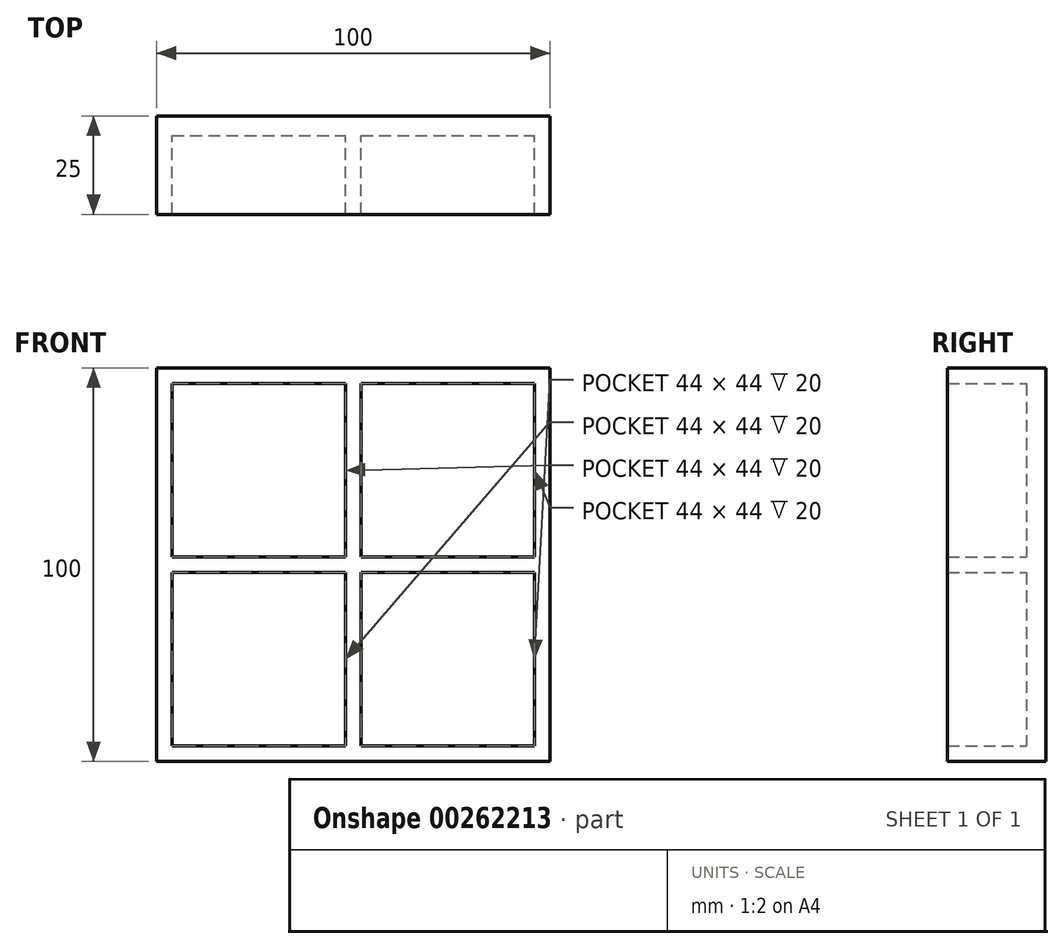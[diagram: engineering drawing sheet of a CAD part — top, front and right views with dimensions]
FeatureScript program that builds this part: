
annotation { "Feature Type Name" : "Feature", "Feature Type Description" : "" }
export const myFeature = defineFeature(function(context is Context, id is Id, definition is map)
    precondition{}
    {
        {
            var Q0;
            Q0=qCreatedBy(makeId("Front.planeOp"),FACE);
            var sketch = newSketch(context, id + "F0", { "sketchPlane" : qUnion([Q0])});
            skLineSegment(sketch, "E0.bottom", {"start": v(-54.06, 49.35) * mm, "end": v(45.94, 49.35) * mm});
            skLineSegment(sketch, "E0.top", {"start": v(-54.06, -50.65) * mm, "end": v(45.94, -50.65) * mm});
            skLineSegment(sketch, "E0.left", {"start": v(-54.06, 49.35) * mm, "end": v(-54.06, -50.65) * mm});
            skLineSegment(sketch, "E0.right", {"start": v(45.94, 49.35) * mm, "end": v(45.94, -50.65) * mm});
            skLineSegment(sketch, "E1", {"start": v(-6.06, 45.35) * mm, "end": v(-6.06, 1.35) * mm});
            skLineSegment(sketch, "E2", {"start": v(-2.06, 45.35) * mm, "end": v(-2.06, 1.35) * mm});
            skLineSegment(sketch, "E3", {"start": v(-50.06, 1.35) * mm, "end": v(-6.06, 1.35) * mm});
            skLineSegment(sketch, "E4", {"start": v(-50.06, -2.65) * mm, "end": v(-6.06, -2.65) * mm});
            skLineSegment(sketch, "E5.trimOffspring", {"start": v(-6.06, -2.65) * mm, "end": v(-6.06, -46.65) * mm});
            skLineSegment(sketch, "E6.trimOffspring", {"start": v(-2.06, 1.35) * mm, "end": v(41.94, 1.35) * mm});
            skLineSegment(sketch, "E7.trimOffspring", {"start": v(-2.06, -2.65) * mm, "end": v(-2.06, -46.65) * mm});
            skLineSegment(sketch, "E8.trimOffspring", {"start": v(-2.06, -2.65) * mm, "end": v(41.94, -2.65) * mm});
            skLineSegment(sketch, "E9", {"start": v(-50.06, 45.35) * mm, "end": v(-50.06, 1.35) * mm});
            skLineSegment(sketch, "E10", {"start": v(-50.06, 45.35) * mm, "end": v(41.94, 45.35) * mm});
            skLineSegment(sketch, "E11", {"start": v(41.94, -46.65) * mm, "end": v(41.94, -2.65) * mm});
            skLineSegment(sketch, "E12", {"start": v(-50.06, -46.65) * mm, "end": v(-6.06, -46.65) * mm});
            skLineSegment(sketch, "E13.trimOffspring", {"start": v(41.94, 1.35) * mm, "end": v(41.94, 45.35) * mm});
            skLineSegment(sketch, "E14.trimOffspring", {"start": v(-2.06, -46.65) * mm, "end": v(41.94, -46.65) * mm});
            skLineSegment(sketch, "E15.trimOffspring", {"start": v(-50.06, -2.65) * mm, "end": v(-50.06, -46.65) * mm});
            skSolve(sketch);
        }
        {
            var Q0;
            Q0=makeQuery(id+"F0.imprint","IMPRINT",FACE,{"disambiguationData":[TD([[makeQuery(id+"F0.imprint","IMPRINT",EDGE,{"derivedFrom":sQuery(id+"F0.wireOp",EDGE,"E0.bottom")}),-1.0]])]});
            extrude(context, id + "F1", {"entities" : qUnion([Q0]), "depth" : 20 * mm});
        }
        {
            var Q0;
            Q0=makeQuery(id+"F1.opExtrude","CAP_FACE",FACE,{"disambiguationData":[OSD([sQuery(id+"F0.wireOp",EDGE,"E0.bottom"),sQuery(id+"F0.wireOp",EDGE,"E0.top"),sQuery(id+"F0.wireOp",EDGE,"E0.left"),sQuery(id+"F0.wireOp",EDGE,"E0.right"),sQuery(id+"F0.wireOp",EDGE,"E1"),sQuery(id+"F0.wireOp",EDGE,"E2"),sQuery(id+"F0.wireOp",EDGE,"E3"),sQuery(id+"F0.wireOp",EDGE,"E4"),sQuery(id+"F0.wireOp",EDGE,"E5.trimOffspring"),sQuery(id+"F0.wireOp",EDGE,"E6.trimOffspring"),sQuery(id+"F0.wireOp",EDGE,"E7.trimOffspring"),sQuery(id+"F0.wireOp",EDGE,"E8.trimOffspring"),sQuery(id+"F0.wireOp",EDGE,"E9"),sQuery(id+"F0.wireOp",EDGE,"E10"),sQuery(id+"F0.wireOp",EDGE,"E11"),sQuery(id+"F0.wireOp",EDGE,"E12"),sQuery(id+"F0.wireOp",EDGE,"E13.trimOffspring"),sQuery(id+"F0.wireOp",EDGE,"E14.trimOffspring"),sQuery(id+"F0.wireOp",EDGE,"E15.trimOffspring")])],"isStart":true});
            var sketch = newSketch(context, id + "F2", { "sketchPlane" : qUnion([Q0])});
            skLineSegment(sketch, "E16.bottom", {"start": v(-45.94, 49.35) * mm, "end": v(54.06, 49.35) * mm});
            skLineSegment(sketch, "E16.top", {"start": v(-45.94, -50.65) * mm, "end": v(54.06, -50.65) * mm});
            skLineSegment(sketch, "E16.left", {"start": v(-45.94, 49.35) * mm, "end": v(-45.94, -50.65) * mm});
            skLineSegment(sketch, "E16.right", {"start": v(54.06, 49.35) * mm, "end": v(54.06, -50.65) * mm});
            skSolve(sketch);
        }
        {
            var Q0;
            Q0 = qSketchRegion(id + "F2", true);
            extrude(context, id + "F3", {"entities" : qUnion([Q0]), "operationType" : NewBodyOperationType.ADD, "depth" : 5 * mm});
        }
    });
